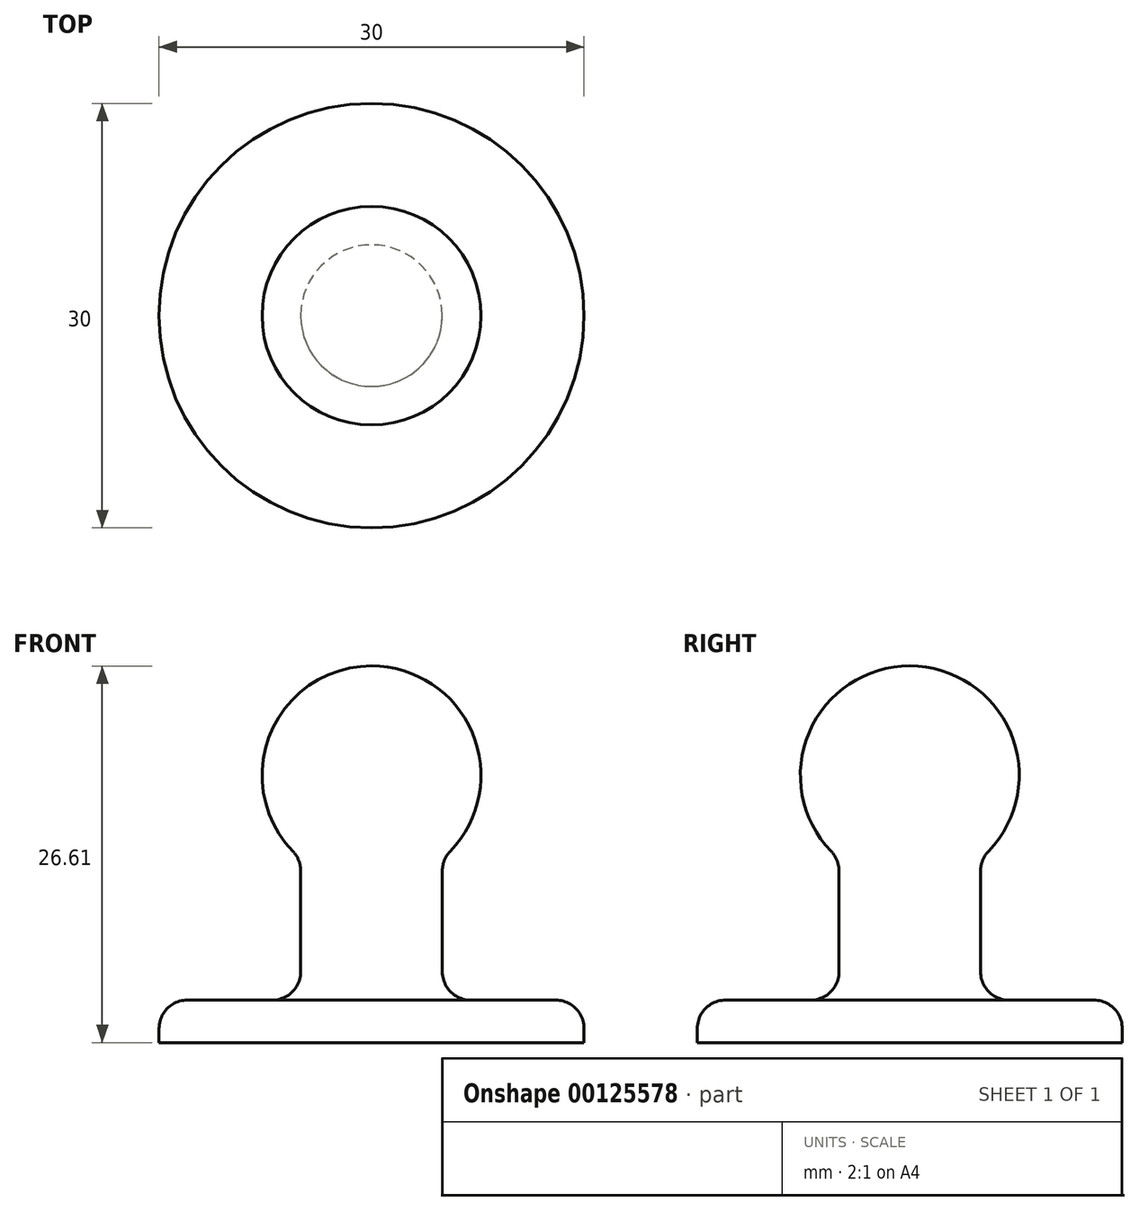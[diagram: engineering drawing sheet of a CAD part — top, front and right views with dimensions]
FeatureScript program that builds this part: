
annotation { "Feature Type Name" : "Feature", "Feature Type Description" : "" }
export const myFeature = defineFeature(function(context is Context, id is Id, definition is map)
    precondition{}
    {
        {
            var Q0;
            Q0=qCreatedBy(makeId("Front.planeOp"),FACE);
            var sketch = newSketch(context, id + "F0", { "sketchPlane" : qUnion([Q0])});
            skLineSegment(sketch, "E0", {"start": v(0, 0) * mm, "end": v(-15, 0) * mm});
            skLineSegment(sketch, "E1", {"start": v(-15, 0) * mm, "end": v(-15, 3) * mm});
            skLineSegment(sketch, "E2", {"start": v(-15, 3) * mm, "end": v(-5, 3) * mm});
            skLineSegment(sketch, "E3", {"start": v(-5, 3) * mm, "end": v(-5, 13) * mm});
            skArc(sketch, "E4", {"start": v(0, 26.61) * mm, "mid": v(-7.25, 21.55) * mm, "end": v(-5, 13) * mm});
            skLineSegment(sketch, "E5", {"start": v(0, 26.61) * mm, "end": v(0, 0) * mm});
            skSolve(sketch);
        }
        {
            var Q0;
            Q0=makeQuery(id+"F0.imprint","IMPRINT",FACE,{"disambiguationData":[TD([[makeQuery(id+"F0.imprint","IMPRINT",EDGE,{"derivedFrom":sQuery(id+"F0.wireOp",EDGE,"E0")}),-1.0]])]});
            var Q1;
            Q1=sQuery(id+"F0.wireOp",EDGE,"E5");
            revolve(context, id + "F1", {"entities" : qUnion([Q0]), "axis" : qUnion([Q1]), "revolveType" : RevolveType.FULL});
        }
        {
            var Q0;
            Q0=makeQuery(id+"F1.opRevolve","SWEPT_EDGE",EDGE,{"disambiguationData":[OSD([sQuery(id+"F0.wireOp",EDGE,"E2"),sQuery(id+"F0.wireOp",EDGE,"E3")])]});
            var Q1;
            Q1=makeQuery(id+"F1.opRevolve","SWEPT_EDGE",EDGE,{"disambiguationData":[OSD([sQuery(id+"F0.wireOp",EDGE,"E3"),sQuery(id+"F0.wireOp",EDGE,"E4")])]});
            var Q2;
            Q2=makeQuery(id+"F1.opRevolve","SWEPT_EDGE",EDGE,{"disambiguationData":[OSD([sQuery(id+"F0.wireOp",EDGE,"E1"),sQuery(id+"F0.wireOp",EDGE,"E2")])]});
            fillet(context, id + "F2", {"entities" : qUnion([Q0, Q1, Q2]), "radius" : 2 * mm, "tangentPropagation" : true, "allowEdgeOverflow" : false});
        }
    });
